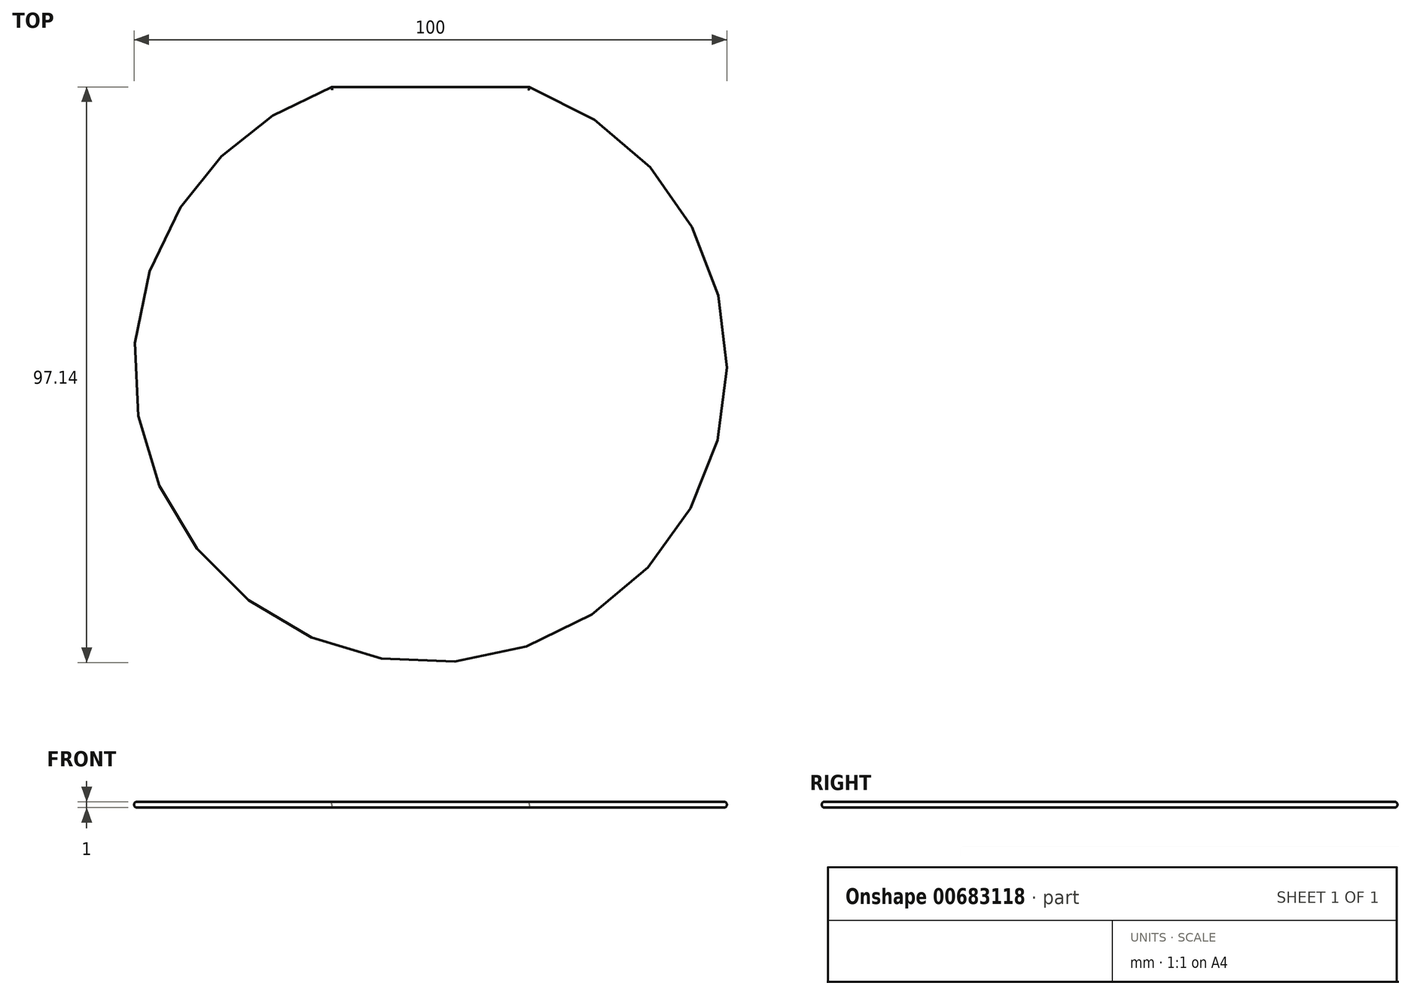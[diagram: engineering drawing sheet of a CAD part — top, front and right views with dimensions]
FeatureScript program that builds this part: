
annotation { "Feature Type Name" : "Feature", "Feature Type Description" : "" }
export const myFeature = defineFeature(function(context is Context, id is Id, definition is map)
    precondition{}
    {
        {
            var Q0;
            Q0=qCreatedBy(makeId("Top.planeOp"),FACE);
            var sketch = newSketch(context, id + "F0", { "sketchPlane" : qUnion([Q0])});
            skArc(sketch, "E0", {"start": v(-17.5, 52.14) * mm, "mid": v(0, -55) * mm, "end": v(17.5, 52.14) * mm, "construction": true});
            skLineSegment(sketch, "E1", {"start": v(-17.5, 52.14) * mm, "end": v(17.5, 52.14) * mm, "construction": true});
            skArc(sketch, "E2.0", {"start": v(-16.66, 47.14) * mm, "mid": v(0, -50) * mm, "end": v(16.66, 47.14) * mm});
            skLineSegment(sketch, "E2.1", {"start": v(-16.66, 47.14) * mm, "end": v(16.66, 47.14) * mm});
            skSolve(sketch);
        }
        {
            var Q0;
            Q0=qSketchRegion(id+"F0",true);
            extrude(context, id + "F1", {"entities" : qUnion([Q0]), "depth" : 1 * mm, "offsetDistance" : 25.4 * mm});
        }
        {
            var Q0;
            Q0=makeQuery(id+"F1.opExtrude","CAP_FACE",FACE,{"disambiguationData":[OSD([sQuery(id+"F0.wireOp",EDGE,"E2.0"),sQuery(id+"F0.wireOp",EDGE,"E2.1")])],"isStart":false});
            var Q1;
            Q1=makeQuery(id+"F1.opExtrude","CAP_FACE",FACE,{"disambiguationData":[OSD([sQuery(id+"F0.wireOp",EDGE,"E2.0"),sQuery(id+"F0.wireOp",EDGE,"E2.1")])],"isStart":true});
            fillet(context, id + "F2", {"entities" : qUnion([Q0, Q1]), "radius" : .5 * mm, "tangentPropagation" : true, "allowEdgeOverflow" : false});
        }
    });
